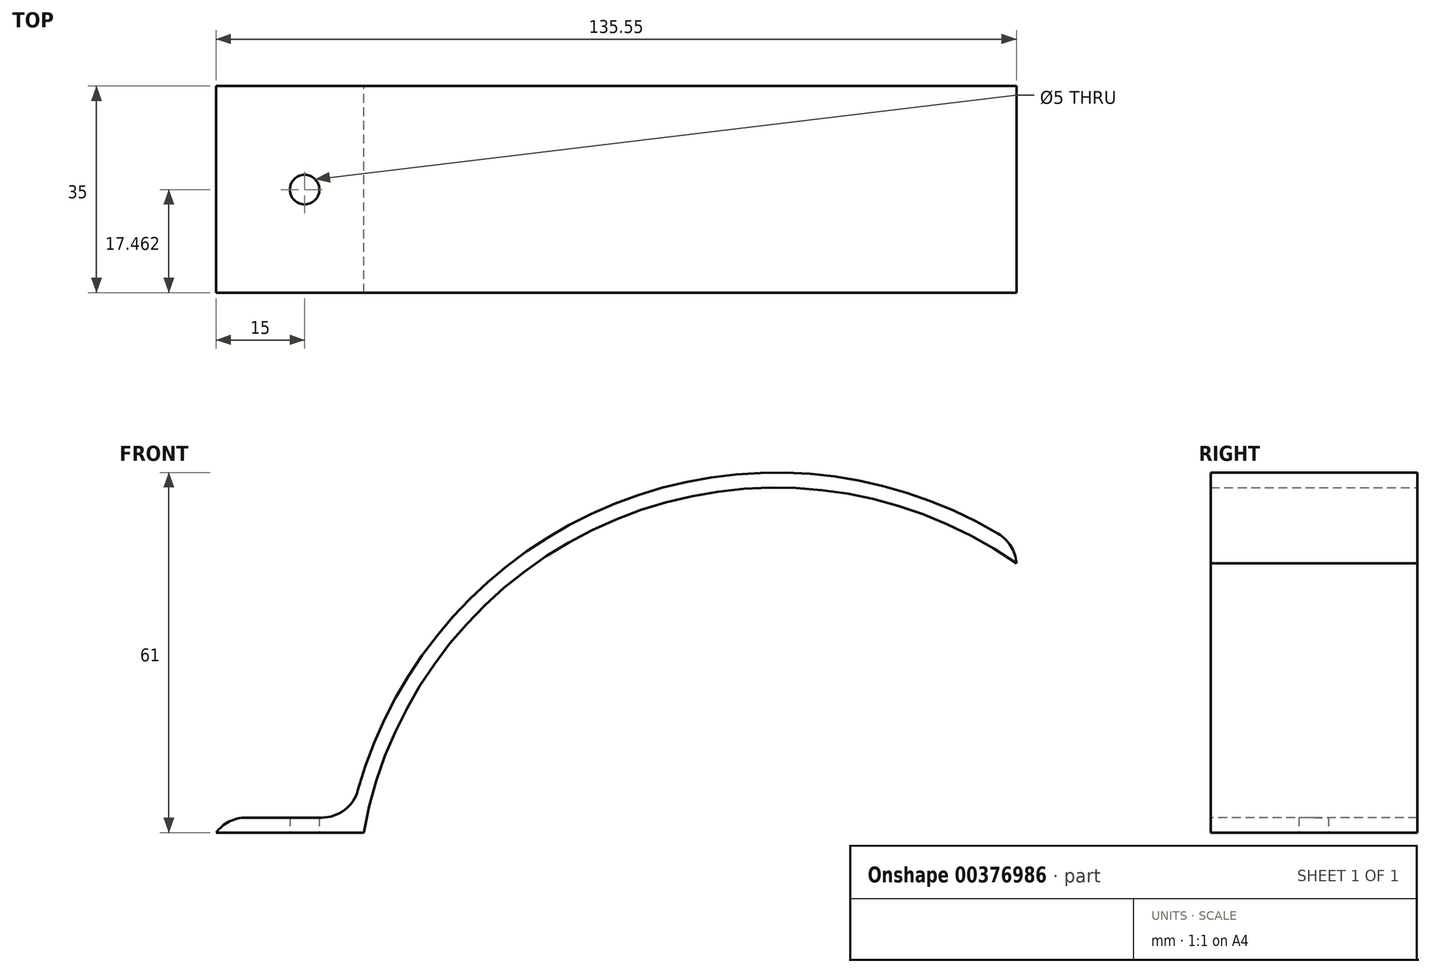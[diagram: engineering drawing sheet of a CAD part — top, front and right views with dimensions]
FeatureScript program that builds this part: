
annotation { "Feature Type Name" : "Feature", "Feature Type Description" : "" }
export const myFeature = defineFeature(function(context is Context, id is Id, definition is map)
    precondition{}
    {
        {
            var Q0;
            Q0=qCreatedBy(makeId("Front.planeOp"),FACE);
            var sketch = newSketch(context, id + "F0", { "sketchPlane" : qUnion([Q0])});
            skLineSegment(sketch, "E0", {"start": v(0, 0) * mm, "end": v(25, 0) * mm});
            skArc(sketch, "E1", {"start": v(135.55, 45.63) * mm, "mid": v(67.78, 53.1) * mm, "end": v(25, 0) * mm});
            skLineSegment(sketch, "E2", {"start": v(0, 0) * mm, "end": v(0, 2.54) * mm});
            skLineSegment(sketch, "E3", {"start": v(0, 2.54) * mm, "end": v(22.9, 2.54) * mm});
            skArc(sketch, "E4", {"start": v(137, 47.7) * mm, "mid": v(67.8, 55.84) * mm, "end": v(22.9, 2.54) * mm});
            skLineSegment(sketch, "E5", {"start": v(137, 47.7) * mm, "end": v(135.55, 45.63) * mm});
            skSolve(sketch);
        }
        {
            var Q0;
            Q0 = qSketchRegion(id + "F0", true);
            extrude(context, id + "F1", {"entities" : qUnion([Q0]), "depth" : 35 * mm});
        }
        {
            var Q0;
            Q0=makeQuery(id+"F1.opExtrude","SWEPT_EDGE",EDGE,{"disambiguationData":[OSD([sQuery(id+"F0.wireOp",EDGE,"E3"),sQuery(id+"F0.wireOp",EDGE,"E4")])]});
            var Q1;
            Q1=makeQuery(id+"F1.opExtrude","SWEPT_EDGE",EDGE,{"disambiguationData":[OSD([sQuery(id+"F0.wireOp",EDGE,"E4"),sQuery(id+"F0.wireOp",EDGE,"E5")])]});
            var Q2;
            Q2=makeQuery(id+"F1.opExtrude","SWEPT_EDGE",EDGE,{"disambiguationData":[OSD([sQuery(id+"F0.wireOp",EDGE,"E2"),sQuery(id+"F0.wireOp",EDGE,"E3")])]});
            fillet(context, id + "F2", {"entities" : qUnion([Q0, Q1, Q2]), "radius" : 6.35 * mm, "tangentPropagation" : true, "allowEdgeOverflow" : false});
        }
        {
            var Q0;
            Q0=makeQuery(id+"F1.opExtrude","SWEPT_FACE",FACE,{"disambiguationData":[OSD([sQuery(id+"F0.wireOp",EDGE,"E0")])]});
            var sketch = newSketch(context, id + "F3", { "sketchPlane" : qUnion([Q0])});
            skCircle(sketch, "E6", {"center": v(15, 17.54) * mm, "radius": 2.5 * mm});
            skSolve(sketch);
        }
        {
            var Q0;
            Q0=makeQuery(id+"F3.imprint","IMPRINT",FACE,{"disambiguationData":[TD([[makeQuery(id+"F3.imprint","IMPRINT",EDGE,{"derivedFrom":sQuery(id+"F3.wireOp",EDGE,"E6")}),1.0]])]});
            extrude(context, id + "F4", {"entities" : qUnion([Q0]), "operationType" : NewBodyOperationType.REMOVE, "endBound" : BoundingType.THROUGH_ALL, "oppositeDirection" : true, "depth" : 25.4 * mm});
        }
    });
